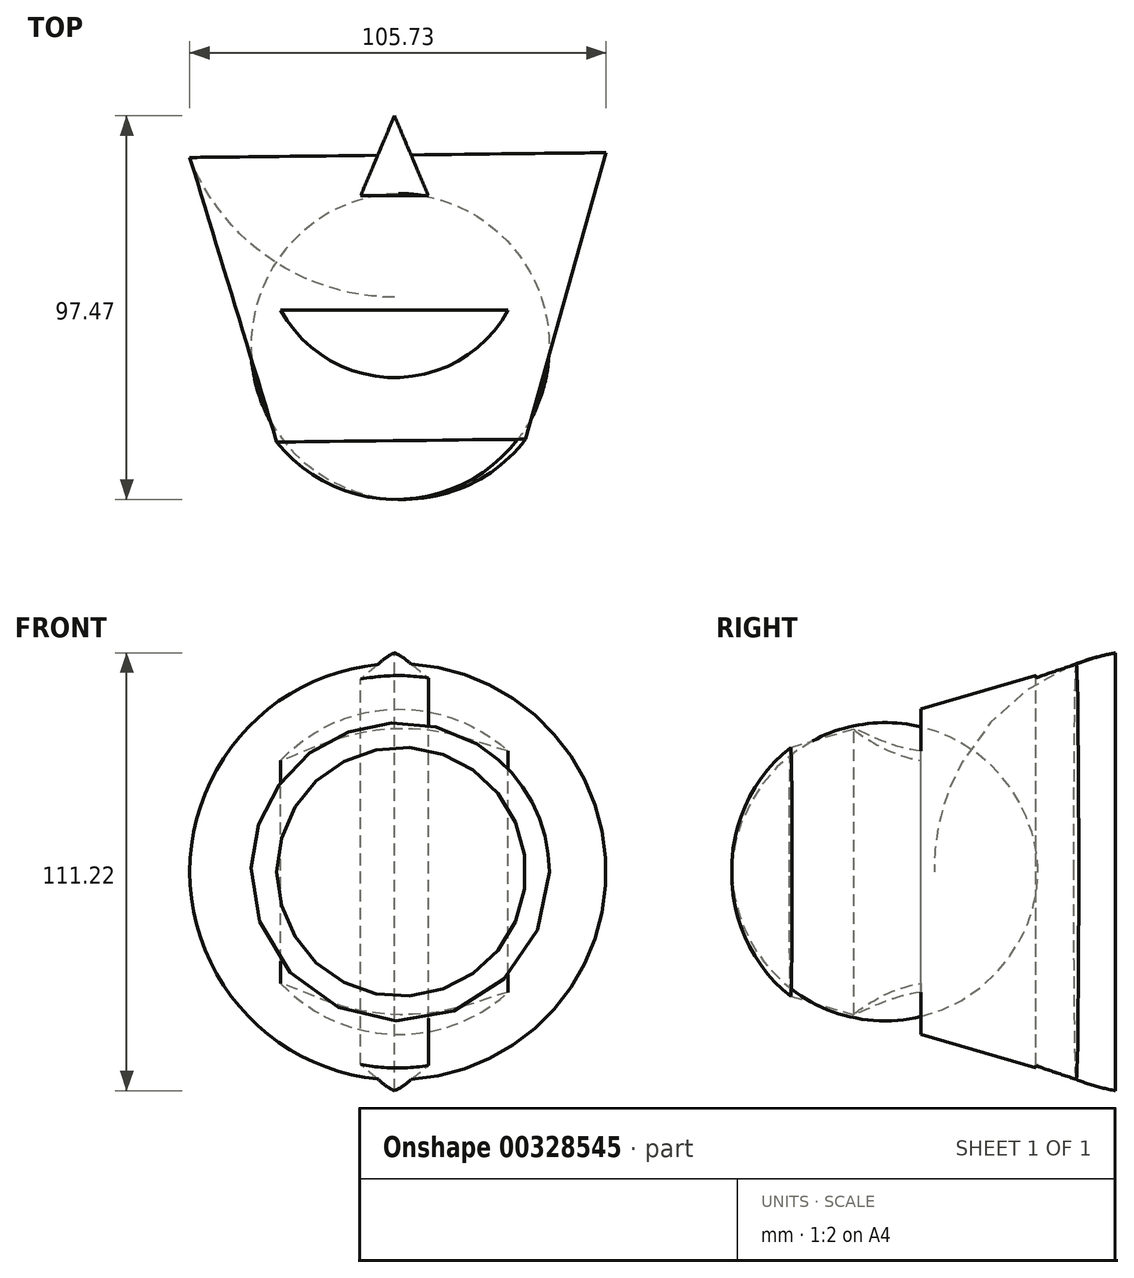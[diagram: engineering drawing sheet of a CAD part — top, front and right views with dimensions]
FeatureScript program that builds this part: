
annotation { "Feature Type Name" : "Feature", "Feature Type Description" : "" }
export const myFeature = defineFeature(function(context is Context, id is Id, definition is map)
    precondition{}
    {
        {
            var Q0;
            Q0=qCreatedBy(makeId("Top.planeOp"),FACE);
            var sketch = newSketch(context, id + "F0", { "sketchPlane" : qUnion([Q0])});
            skArc(sketch, "E0", {"start": v(50.42, 19.26) * mm, "mid": v(1.97, 99.02) * mm, "end": v(-51.99, 22.89) * mm});
            skLineSegment(sketch, "E1", {"start": v(-51.99, 22.89) * mm, "end": v(-29.9, -49.42) * mm});
            skLineSegment(sketch, "E2", {"start": v(30.8, -49.42) * mm, "end": v(50.42, 19.26) * mm});
            skLineSegment(sketch, "E3", {"start": v(0, 8.99) * mm, "end": v(0, 29.31) * mm});
            skLineSegment(sketch, "E4", {"start": v(0, 99.06) * mm, "end": v(1.97, -71.45) * mm});
            skPoint(sketch, "E4.endSnap0", {"position": v(1.97, 99.02) * mm});
            skArc(sketch, "E5", {"start": v(-29.9, -49.42) * mm, "mid": v(0.44, -64) * mm, "end": v(30.8, -49.42) * mm});
            skSolve(sketch);
        }
        {
            var Q0;
            {var subQ10=sQuery(id+"F0.wireOp",EDGE,"E1");Q0=makeQuery(id+"F0.imprint","IMPRINT",FACE,{"disambiguationData":[TD([[makeQuery(id+"F0.imprint","IMPRINT",EDGE,{"derivedFrom":subQ10}),1.0]])]});}
            var Q1;
            Q1=sQuery(id+"F0.wireOp",EDGE,"E4");
            revolve(context, id + "F1", {"entities" : qUnion([Q0]), "axis" : qUnion([Q1]), "revolveType" : RevolveType.FULL});
        }
        {
            var Q0;
            Q0=qCreatedBy(makeId("Top.planeOp"),FACE);
            var sketch = newSketch(context, id + "F2", { "sketchPlane" : qUnion([Q0])});
            skArc(sketch, "E6", {"start": v(-32.42, 52.9) * mm, "mid": v(-20.98, 43.12) * mm, "end": v(-10.36, 53.78) * mm});
            skArc(sketch, "E7", {"start": v(-10.36, 53.78) * mm, "mid": v(-21.61, 58.94) * mm, "end": v(-32.42, 52.9) * mm});
            skLineSegment(sketch, "E8", {"start": v(0, 33.48) * mm, "end": v(-8.6, 13.18) * mm});
            skLineSegment(sketch, "E9", {"start": v(-8.6, 13.18) * mm, "end": v(5.52, 13.18) * mm});
            skLineSegment(sketch, "E10", {"start": v(-28.9, -15.94) * mm, "end": v(28.9, -15.94) * mm});
            skArc(sketch, "E11", {"start": v(-28.9, -15.94) * mm, "mid": v(0, -33.02) * mm, "end": v(28.9, -15.94) * mm});
            skArc(sketch, "E12.MirrorCS", {"start": v(10.36, 53.78) * mm, "mid": v(21.61, 58.94) * mm, "end": v(32.42, 52.9) * mm});
            skArc(sketch, "E13.MirrorCS", {"start": v(32.42, 52.9) * mm, "mid": v(20.98, 43.12) * mm, "end": v(10.36, 53.78) * mm});
            skLineSegment(sketch, "E14.MirrorCS", {"start": v(0, 33.48) * mm, "end": v(8.6, 13.18) * mm});
            skLineSegment(sketch, "E15.MirrorCS", {"start": v(8.6, 13.18) * mm, "end": v(-5.52, 13.18) * mm});
            skLineSegment(sketch, "E16", {"start": v(-14.84, -15.94) * mm, "end": v(-14.84, -29.5) * mm});
            skLineSegment(sketch, "E17", {"start": v(0, -15.94) * mm, "end": v(0, -33.02) * mm});
            skLineSegment(sketch, "E18", {"start": v(17.07, -15.94) * mm, "end": v(17.07, -28.27) * mm});
            skLineSegment(sketch, "E19", {"start": v(-23.94, -22.72) * mm, "end": v(23.96, -22.72) * mm});
            skPoint(sketch, "E19.startSnap0", {"position": v(-14.84, -22.72) * mm});
            skSolve(sketch);
        }
        {
            var Q0;
            Q0 = qSketchRegion(id + "F2", true);
            extrude(context, id + "F3", {"entities" : qUnion([Q0]), "operationType" : NewBodyOperationType.REMOVE, "oppositeDirection" : true, "depth" : 112.01 * mm});
        }
        {
            var Q0;
            Q0 = qSketchRegion(id + "F2", true);
            extrude(context, id + "F4", {"entities" : qUnion([Q0]), "operationType" : NewBodyOperationType.REMOVE, "depth" : 95.5 * mm});
        }
        {
            var Q0;
            Q0=qCreatedBy(makeId("Right.planeOp"),FACE);
            var sketch = newSketch(context, id + "F5", { "sketchPlane" : qUnion([Q0])});
            skCircle(sketch, "E20", {"center": v(54.84, 0) * mm, "radius": 6.35 * mm});
            skSolve(sketch);
        }
        {
            var Q0;
            Q0 = qSketchRegion(id + "F5", true);
            extrude(context, id + "F6", {"entities" : qUnion([Q0]), "operationType" : NewBodyOperationType.REMOVE, "oppositeDirection" : true, "depth" : 103.63 * mm});
        }
        {
            var Q0;
            Q0 = qSketchRegion(id + "F5", true);
            extrude(context, id + "F7", {"entities" : qUnion([Q0]), "operationType" : NewBodyOperationType.REMOVE, "depth" : 82.3 * mm});
        }
    });
